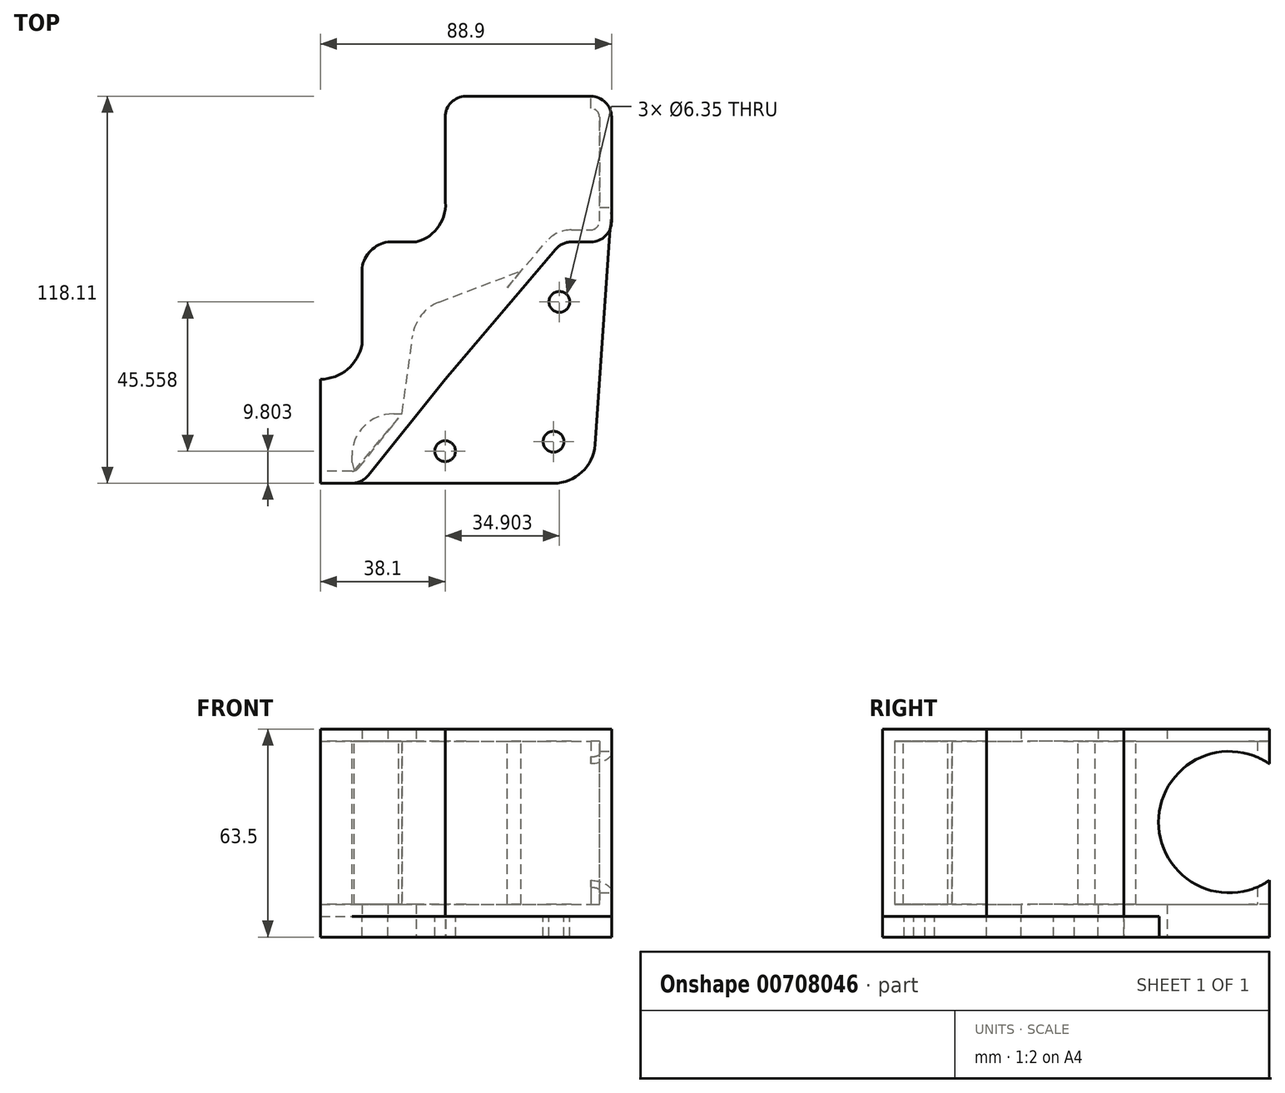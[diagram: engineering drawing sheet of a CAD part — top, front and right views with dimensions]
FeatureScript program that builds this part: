
annotation { "Feature Type Name" : "Feature", "Feature Type Description" : "" }
export const myFeature = defineFeature(function(context is Context, id is Id, definition is map)
    precondition{}
    {
        {
            var Q0;
            Q0=qCreatedBy(makeId("Top.planeOp"),FACE);
            var sketch = newSketch(context, id + "F0", { "sketchPlane" : qUnion([Q0])});
            skLineSegment(sketch, "E0.bottom", {"start": v(38.56, 0) * mm, "end": v(44.45, 0) * mm});
            skLineSegment(sketch, "E0.top", {"start": v(6.35, 44.45) * mm, "end": v(44.45, 44.45) * mm});
            skLineSegment(sketch, "E0.left", {"start": v(0, 9.64) * mm, "end": v(0, 38.1) * mm});
            skLineSegment(sketch, "E0.right", {"start": v(50.8, 6.35) * mm, "end": v(50.8, 38.1) * mm});
            skLineSegment(sketch, "E1.bottom", {"start": v(-8.79, 0) * mm, "end": v(-17.46, 0) * mm});
            skLineSegment(sketch, "E1.right", {"start": v(-25.4, -7.9) * mm, "end": v(-25.4, -31.29) * mm});
            skLineSegment(sketch, "E2.top", {"start": v(-28.45, -73.66) * mm, "end": v(-38.1, -73.66) * mm});
            skLineSegment(sketch, "E2.right", {"start": v(-38.1, -41.91) * mm, "end": v(-38.1, -73.66) * mm});
            skLineSegment(sketch, "E3", {"start": v(-23.5, -71.28) * mm, "end": v(0, -41.91) * mm});
            skLineSegment(sketch, "E4", {"start": v(0, -41.91) * mm, "end": v(33.72, -2.24) * mm});
            skArc(sketch, "E5", {"start": v(-38.1, -41.91) * mm, "mid": v(-29.82, -38.9) * mm, "end": v(-25.4, -31.29) * mm});
            skArc(sketch, "E6", {"start": v(-17.46, 0) * mm, "mid": v(-22.7, -2.67) * mm, "end": v(-25.4, -7.9) * mm});
            skArc(sketch, "E7", {"start": v(-8.79, 0) * mm, "mid": v(-1.83, 4.92) * mm, "end": v(0, 13.24) * mm});
            skPoint(sketch, "E8.visualSharp", {"position": v(0, 44.45) * mm});
            skArc(sketch, "E8.filletArc", {"start": v(6.35, 44.45) * mm, "mid": v(1.86, 42.6) * mm, "end": v(0, 38.1) * mm});
            skPoint(sketch, "E9.visualSharp", {"position": v(50.8, 44.45) * mm});
            skArc(sketch, "E9.filletArc", {"start": v(50.8, 38.1) * mm, "mid": v(48.94, 42.6) * mm, "end": v(44.45, 44.45) * mm});
            skPoint(sketch, "E10.visualSharp", {"position": v(50.8, 0) * mm});
            skArc(sketch, "E10.filletArc", {"start": v(44.45, 0) * mm, "mid": v(48.94, 1.86) * mm, "end": v(50.8, 6.35) * mm});
            skPoint(sketch, "E11.visualSharp", {"position": v(35.62, 0) * mm});
            skArc(sketch, "E11.filletArc", {"start": v(38.56, 0) * mm, "mid": v(35.9, -0.59) * mm, "end": v(33.72, -2.24) * mm});
            skPoint(sketch, "E12.visualSharp", {"position": v(-25.4, -73.66) * mm});
            skArc(sketch, "E12.filletArc", {"start": v(-28.45, -73.66) * mm, "mid": v(-25.7, -73.03) * mm, "end": v(-23.5, -71.28) * mm});
            skSolve(sketch);
        }
        {
            var Q0;
            Q0=makeQuery(id+"F0.imprint","IMPRINT",FACE,{"disambiguationData":[TD([[makeQuery(id+"F0.imprint","IMPRINT",EDGE,{"derivedFrom":sQuery(id+"F0.wireOp",EDGE,"E0.bottom")}),1.0]])]});
            extrude(context, id + "F1", {"entities" : qUnion([Q0]), "depth" : 57.15 * mm, "offsetDistance" : 25.4 * mm});
        }
        {
            var Q0;
            Q0=makeQuery(id+"F1.opExtrude","SWEPT_FACE",FACE,{"disambiguationData":[OSD([sQuery(id+"F0.wireOp",EDGE,"E0.left")])]});
            var Q1;
            Q1=makeQuery(id+"F1.opExtrude","SWEPT_FACE",FACE,{"disambiguationData":[OSD([sQuery(id+"F0.wireOp",EDGE,"E8.filletArc")])]});
            var Q2;
            Q2=makeQuery(id+"F1.opExtrude","SWEPT_FACE",FACE,{"disambiguationData":[OSD([sQuery(id+"F0.wireOp",EDGE,"E0.top")])]});
            var Q3;
            Q3=makeQuery(id+"F1.opExtrude","SWEPT_FACE",FACE,{"disambiguationData":[OSD([sQuery(id+"F0.wireOp",EDGE,"E7")])]});
            var Q4;
            Q4=makeQuery(id+"F1.opExtrude","SWEPT_FACE",FACE,{"disambiguationData":[OSD([sQuery(id+"F0.wireOp",EDGE,"E1.bottom")])]});
            var Q5;
            Q5=makeQuery(id+"F1.opExtrude","SWEPT_FACE",FACE,{"disambiguationData":[OSD([sQuery(id+"F0.wireOp",EDGE,"E6")])]});
            var Q6;
            Q6=makeQuery(id+"F1.opExtrude","SWEPT_FACE",FACE,{"disambiguationData":[OSD([sQuery(id+"F0.wireOp",EDGE,"E1.right")])]});
            var Q7;
            Q7=makeQuery(id+"F1.opExtrude","SWEPT_FACE",FACE,{"disambiguationData":[OSD([sQuery(id+"F0.wireOp",EDGE,"E5")])]});
            var Q8;
            Q8=makeQuery(id+"F1.opExtrude","SWEPT_FACE",FACE,{"disambiguationData":[OSD([sQuery(id+"F0.wireOp",EDGE,"E2.right")])]});
            shell(context, id + "F2", {"entities" : qUnion([Q0, Q1, Q2, Q3, Q4, Q5, Q6, Q7, Q8]), "thickness" : 3.68 * mm});
        }
        {
            var Q0;
            Q0=makeQuery(id+"F1.opExtrude","SWEPT_FACE",FACE,{"disambiguationData":[OSD([sQuery(id+"F0.wireOp",EDGE,"E0.right")])]});
            var sketch = newSketch(context, id + "F3", { "sketchPlane" : qUnion([Q0])});
            skLineSegment(sketch, "E13", {"start": v(6.35, 57.15) * mm, "end": v(44.75, 0) * mm, "construction": true});
            skLineSegment(sketch, "E14", {"start": v(6.35, 0) * mm, "end": v(44.36, 57.17) * mm, "construction": true});
            skLineSegment(sketch, "E15", {"start": v(25.45, 28.72) * mm, "end": v(32.2, 28.72) * mm, "construction": true});
            skCircle(sketch, "E16", {"center": v(32.2, 28.72) * mm, "radius": 21.59 * mm});
            skSolve(sketch);
        }
        {
            var Q0;
            {var subQ0=sQuery(id+"F3.wireOp",EDGE,"E16");var subQ1=makeQuery(id+"F1.opExtrude","SWEPT_EDGE",EDGE,{"disambiguationData":[OSD([sQuery(id+"F0.wireOp",EDGE,"E0.right"),sQuery(id+"F0.wireOp",EDGE,"E9.filletArc")])]});var subQ2=makeQuery(id+"F3.imprint","INTERSECT",VERTEX,{"disambiguationData":[OD(0.0)],"derivedFrom":[subQ1,subQ0]});Q0=makeQuery(id+"F3.imprint","IMPRINT",FACE,{"disambiguationData":[TD([[makeQuery(id+"F3.imprint","IMPRINT",EDGE,{"disambiguationData":[TD([[subQ2,-1.0]])],"derivedFrom":subQ0}),1.0]])]});}
            var Q1;
            {var subQ0=sQuery(id+"F3.wireOp",EDGE,"E16");var subQ1=makeQuery(id+"F1.opExtrude","SWEPT_EDGE",EDGE,{"disambiguationData":[OSD([sQuery(id+"F0.wireOp",EDGE,"E0.right"),sQuery(id+"F0.wireOp",EDGE,"E9.filletArc")])]});var subQ2=makeQuery(id+"F3.imprint","INTERSECT",VERTEX,{"disambiguationData":[OD(0.0)],"derivedFrom":[subQ1,subQ0]});Q1=makeQuery(id+"F3.imprint","IMPRINT",FACE,{"disambiguationData":[TD([[makeQuery(id+"F3.imprint","IMPRINT",EDGE,{"disambiguationData":[TD([[subQ2,1.0]])],"derivedFrom":subQ0}),1.0]])]});}
            extrude(context, id + "F4", {"entities" : qUnion([Q0, Q1]), "operationType" : NewBodyOperationType.REMOVE, "oppositeDirection" : true, "depth" : 25.4 * mm, "offsetDistance" : 25.4 * mm});
        }
        {
            var Q0;
            Q0=makeQuery(id+"F1.opExtrude","CAP_FACE",FACE,{"disambiguationData":[OSD([sQuery(id+"F0.wireOp",EDGE,"E0.bottom"),sQuery(id+"F0.wireOp",EDGE,"E0.top"),sQuery(id+"F0.wireOp",EDGE,"E0.left"),sQuery(id+"F0.wireOp",EDGE,"E0.right"),sQuery(id+"F0.wireOp",EDGE,"E1.bottom"),sQuery(id+"F0.wireOp",EDGE,"E1.right"),sQuery(id+"F0.wireOp",EDGE,"E2.top"),sQuery(id+"F0.wireOp",EDGE,"E2.right"),sQuery(id+"F0.wireOp",EDGE,"E3"),sQuery(id+"F0.wireOp",EDGE,"E4"),sQuery(id+"F0.wireOp",EDGE,"E5"),sQuery(id+"F0.wireOp",EDGE,"E6"),sQuery(id+"F0.wireOp",EDGE,"E7"),sQuery(id+"F0.wireOp",EDGE,"E8.filletArc"),sQuery(id+"F0.wireOp",EDGE,"E9.filletArc"),sQuery(id+"F0.wireOp",EDGE,"E10.filletArc"),sQuery(id+"F0.wireOp",EDGE,"E11.filletArc"),sQuery(id+"F0.wireOp",EDGE,"E12.filletArc")])],"isStart":true});
            var sketch = newSketch(context, id + "F5", { "sketchPlane" : qUnion([Q0])});
            skLineSegment(sketch, "E17", {"start": v(-38.1, 73.66) * mm, "end": v(33.1, 73.66) * mm});
            skLineSegment(sketch, "E18", {"start": v(45.78, 61.84) * mm, "end": v(50.8, -10.87) * mm});
            skLineSegment(sketch, "E19", {"start": v(50.8, -10.87) * mm, "end": v(50.8, -38.1) * mm});
            skArc(sketch, "E20", {"start": v(44.45, -44.45) * mm, "mid": v(48.94, -42.6) * mm, "end": v(50.8, -38.1) * mm});
            skLineSegment(sketch, "E21", {"start": v(44.45, -44.45) * mm, "end": v(6.35, -44.45) * mm});
            skArc(sketch, "E22", {"start": v(0, -38.1) * mm, "mid": v(1.86, -42.6) * mm, "end": v(6.35, -44.45) * mm});
            skLineSegment(sketch, "E23", {"start": v(0, -38.1) * mm, "end": v(0, -13.24) * mm});
            skArc(sketch, "E24", {"start": v(0, -13.24) * mm, "mid": v(-1.85, -4.93) * mm, "end": v(-8.79, 0) * mm});
            skLineSegment(sketch, "E25", {"start": v(-8.79, 0) * mm, "end": v(-17.46, 0) * mm});
            skArc(sketch, "E26", {"start": v(-25.4, 7.9) * mm, "mid": v(-22.6, 2.77) * mm, "end": v(-17.46, 0) * mm});
            skLineSegment(sketch, "E27", {"start": v(-25.4, 7.9) * mm, "end": v(-25.4, 31.29) * mm});
            skArc(sketch, "E28", {"start": v(-25.4, 31.29) * mm, "mid": v(-29.75, 38.98) * mm, "end": v(-38.1, 41.91) * mm});
            skLineSegment(sketch, "E29", {"start": v(-38.1, 41.91) * mm, "end": v(-38.1, 73.66) * mm});
            skPoint(sketch, "E30.visualSharp", {"position": v(44.96, 73.66) * mm});
            skArc(sketch, "E30.filletArc", {"start": v(45.78, 61.84) * mm, "mid": v(41.77, 70.24) * mm, "end": v(33.1, 73.66) * mm});
            skSolve(sketch);
        }
        {
            var Q0;
            {var subQ5=makeQuery(id+"F1.opExtrude","CAP_EDGE",EDGE,{"disambiguationData":[OSD([sQuery(id+"F0.wireOp",EDGE,"E0.bottom")])],"isStart":true});Q0=makeQuery(id+"F5.imprint","IMPRINT",FACE,{"disambiguationData":[TD([[makeQuery(id+"F5.imprint","IMPRINT",EDGE,{"derivedFrom":subQ5}),1.0]])]});}
            var Q1;
            {var subQ3=sQuery(id+"F5.wireOp",EDGE,"E19");Q1=makeQuery(id+"F5.imprint","IMPRINT",FACE,{"disambiguationData":[TD([[makeQuery(id+"F5.imprint","IMPRINT",EDGE,{"derivedFrom":subQ3}),-1.0]])]});}
            extrude(context, id + "F6", {"entities" : qUnion([Q0, Q1]), "operationType" : NewBodyOperationType.ADD, "depth" : 6.35 * mm, "offsetDistance" : 25.4 * mm});
        }
        {
            var Q0;
            Q0=makeQuery(id+"F6.opExtrude","CAP_FACE",FACE,{"disambiguationData":[OSD([sQuery(id+"F0.wireOp",EDGE,"E7"),sQuery(id+"F5.wireOp",EDGE,"E17"),sQuery(id+"F5.wireOp",EDGE,"E18"),sQuery(id+"F5.wireOp",EDGE,"E19"),sQuery(id+"F5.wireOp",EDGE,"E20"),sQuery(id+"F5.wireOp",EDGE,"E21"),sQuery(id+"F5.wireOp",EDGE,"E22"),sQuery(id+"F5.wireOp",EDGE,"E23"),sQuery(id+"F5.wireOp",EDGE,"E25"),sQuery(id+"F5.wireOp",EDGE,"E26"),sQuery(id+"F5.wireOp",EDGE,"E27"),sQuery(id+"F5.wireOp",EDGE,"E28"),sQuery(id+"F5.wireOp",EDGE,"E29"),sQuery(id+"F5.wireOp",EDGE,"E30.filletArc")])],"isStart":true});
            var sketch = newSketch(context, id + "F7", { "sketchPlane" : qUnion([Q0])});
            skCircle(sketch, "E31", {"center": v(0, -63.86) * mm, "radius": 3.18 * mm});
            skCircle(sketch, "E32", {"center": v(34.9, -18.3) * mm, "radius": 3.18 * mm});
            skCircle(sketch, "E33", {"center": v(33.1, -60.96) * mm, "radius": 3.18 * mm});
            skSolve(sketch);
        }
        {
            var Q0;
            Q0=makeQuery(id+"F7.imprint","IMPRINT",FACE,{"disambiguationData":[TD([[makeQuery(id+"F7.imprint","IMPRINT",EDGE,{"derivedFrom":sQuery(id+"F7.wireOp",EDGE,"E31")}),1.0]])]});
            var Q1;
            Q1=makeQuery(id+"F7.imprint","IMPRINT",FACE,{"disambiguationData":[TD([[makeQuery(id+"F7.imprint","IMPRINT",EDGE,{"derivedFrom":sQuery(id+"F7.wireOp",EDGE,"E33")}),1.0]])]});
            var Q2;
            Q2=makeQuery(id+"F7.imprint","IMPRINT",FACE,{"disambiguationData":[TD([[makeQuery(id+"F7.imprint","IMPRINT",EDGE,{"derivedFrom":sQuery(id+"F7.wireOp",EDGE,"E32")}),1.0]])]});
            extrude(context, id + "F8", {"entities" : qUnion([Q0, Q1, Q2]), "operationType" : NewBodyOperationType.REMOVE, "oppositeDirection" : true, "depth" : 25.4 * mm, "offsetDistance" : 25.4 * mm});
        }
        {
            var Q0;
            Q0=makeQuery(id+"F1.opExtrude","CAP_FACE",FACE,{"disambiguationData":[OSD([sQuery(id+"F0.wireOp",EDGE,"E0.bottom"),sQuery(id+"F0.wireOp",EDGE,"E0.top"),sQuery(id+"F0.wireOp",EDGE,"E0.left"),sQuery(id+"F0.wireOp",EDGE,"E0.right"),sQuery(id+"F0.wireOp",EDGE,"E1.bottom"),sQuery(id+"F0.wireOp",EDGE,"E1.right"),sQuery(id+"F0.wireOp",EDGE,"E2.top"),sQuery(id+"F0.wireOp",EDGE,"E2.right"),sQuery(id+"F0.wireOp",EDGE,"E3"),sQuery(id+"F0.wireOp",EDGE,"E4"),sQuery(id+"F0.wireOp",EDGE,"E5"),sQuery(id+"F0.wireOp",EDGE,"E6"),sQuery(id+"F0.wireOp",EDGE,"E7"),sQuery(id+"F0.wireOp",EDGE,"E8.filletArc"),sQuery(id+"F0.wireOp",EDGE,"E9.filletArc"),sQuery(id+"F0.wireOp",EDGE,"E10.filletArc"),sQuery(id+"F0.wireOp",EDGE,"E11.filletArc"),sQuery(id+"F0.wireOp",EDGE,"E12.filletArc")])],"isStart":false});
            var sketch = newSketch(context, id + "F9", { "sketchPlane" : qUnion([Q0])});
            skLineSegment(sketch, "E34", {"start": v(-28.45, -67.31) * mm, "end": v(-28.45, -65.2) * mm});
            skLineSegment(sketch, "E35", {"start": v(-15.75, -52.5) * mm, "end": v(-13.13, -52.5) * mm});
            skLineSegment(sketch, "E36", {"start": v(-13.13, -52.5) * mm, "end": v(-9.9, -28.51) * mm});
            skLineSegment(sketch, "E37", {"start": v(-1.83, -18.34) * mm, "end": v(23.21, -8.8) * mm});
            skLineSegment(sketch, "E38", {"start": v(23.21, -8.8) * mm, "end": v(-13.13, -52.5) * mm});
            skLineSegment(sketch, "E39", {"start": v(-28.45, -67.31) * mm, "end": v(-27.72, -69.84) * mm});
            skLineSegment(sketch, "E40", {"start": v(-27.72, -69.84) * mm, "end": v(-13.13, -52.5) * mm});
            skPoint(sketch, "E41.visualSharp", {"position": v(-8.89, -21.03) * mm});
            skArc(sketch, "E41.filletArc", {"start": v(-1.83, -18.34) * mm, "mid": v(-7.26, -22.32) * mm, "end": v(-9.9, -28.51) * mm});
            skPoint(sketch, "E42.visualSharp", {"position": v(-28.45, -52.5) * mm});
            skArc(sketch, "E42.filletArc", {"start": v(-15.75, -52.5) * mm, "mid": v(-24.73, -56.21) * mm, "end": v(-28.45, -65.2) * mm});
            skSolve(sketch);
        }
        {
            var Q0;
            Q0=makeQuery(id+"F9.imprint","IMPRINT",FACE,{"disambiguationData":[TD([[makeQuery(id+"F9.imprint","IMPRINT",EDGE,{"derivedFrom":sQuery(id+"F9.wireOp",EDGE,"E36")}),-1.0]])]});
            var Q1;
            Q1=makeQuery(id+"F9.imprint","IMPRINT",FACE,{"disambiguationData":[TD([[makeQuery(id+"F9.imprint","IMPRINT",EDGE,{"derivedFrom":sQuery(id+"F9.wireOp",EDGE,"E34")}),-1.0]])]});
            extrude(context, id + "F10", {"entities" : qUnion([Q0, Q1]), "operationType" : NewBodyOperationType.ADD, "oppositeDirection" : true, "depth" : 56.64 * mm, "offsetDistance" : 25.4 * mm});
        }
    });
